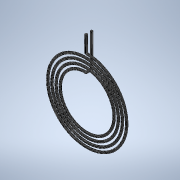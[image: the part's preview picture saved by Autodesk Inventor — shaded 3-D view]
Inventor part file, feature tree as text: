
AUTODESK INVENTOR PART (.ipt)
format: ipt  version: 2022 (Build 260153000, 153)  size: 274,944 bytes
history: native  units: in
note: dims shown in document units (in); Inventor stores cm internally (conversion verified against a paired STEP export)
features: other x2, sketch x1
ambient origin geometry x8: Origin, YZ Plane, XZ Plane, XY Plane, X Axis, Y Axis, Z Axis, Center Point
feature tree (3):
  other  "Heating-Coil_Half_Scale"
  sketch  "Sketch1"  dims[d0=7.5in d1=0.8463in]
  other  "MeshFeature1"
